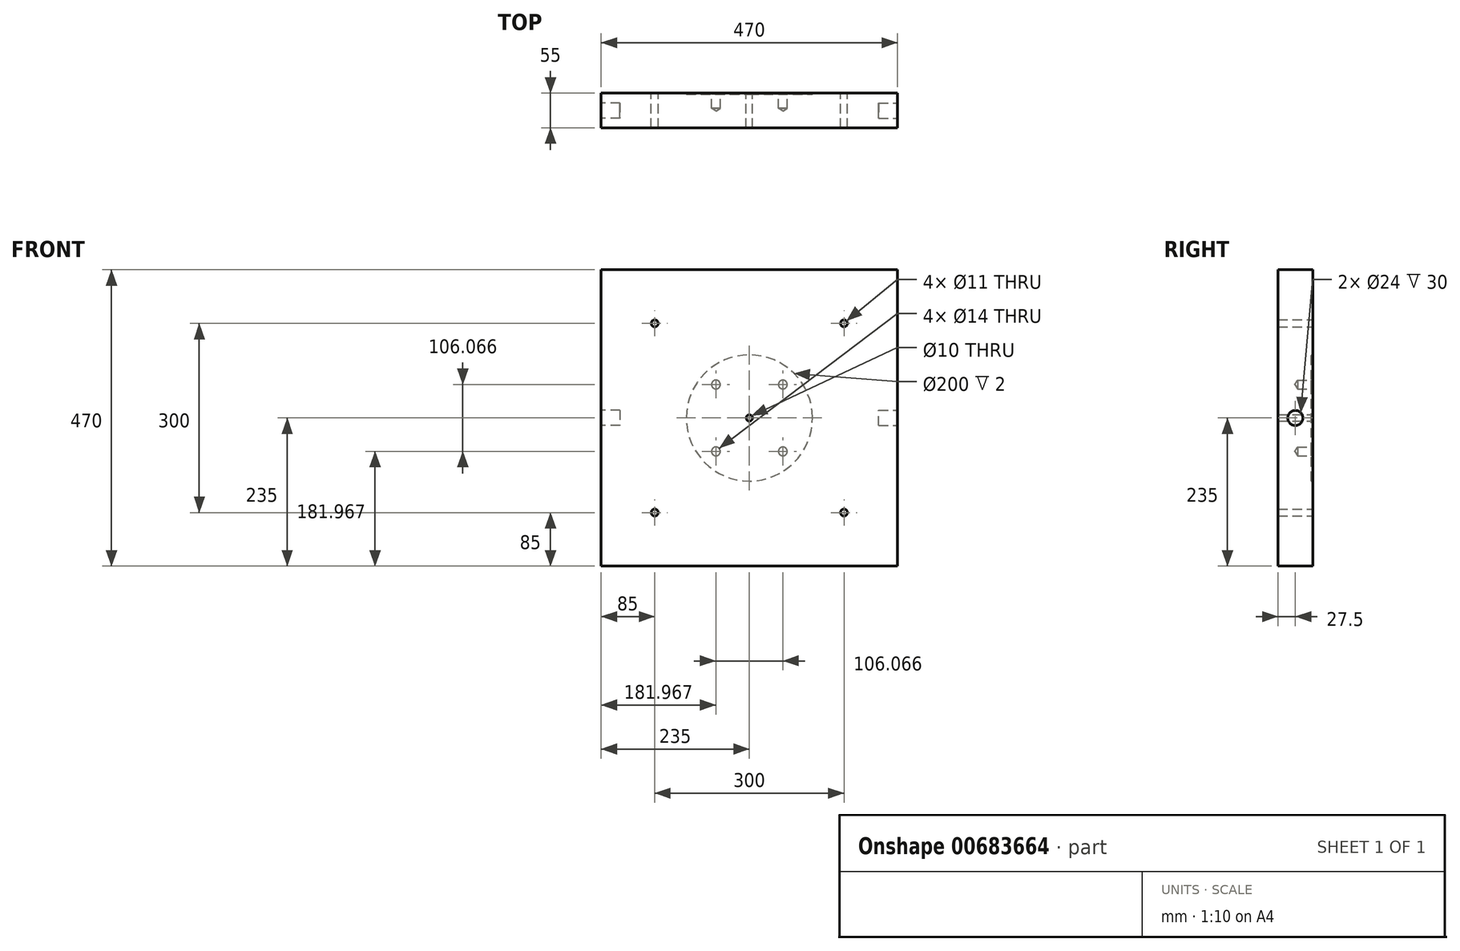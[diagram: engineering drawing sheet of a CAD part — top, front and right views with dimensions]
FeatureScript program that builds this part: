
annotation { "Feature Type Name" : "Feature", "Feature Type Description" : "" }
export const myFeature = defineFeature(function(context is Context, id is Id, definition is map)
    precondition{}
    {
        {
            var Q0;
            Q0=qCreatedBy(makeId("Front.planeOp"),FACE);
            var sketch = newSketch(context, id + "F0", { "sketchPlane" : qUnion([Q0])});
            skLineSegment(sketch, "E0.bottom", {"start": v(235, 235) * mm, "end": v(-235, 235) * mm});
            skLineSegment(sketch, "E0.top", {"start": v(235, -235) * mm, "end": v(-235, -235) * mm});
            skLineSegment(sketch, "E0.left", {"start": v(235, 235) * mm, "end": v(235, -235) * mm});
            skLineSegment(sketch, "E0.right", {"start": v(-235, 235) * mm, "end": v(-235, -235) * mm});
            skPoint(sketch, "E0.middle", {"position": v(0, 0) * mm});
            skCircle(sketch, "E1", {"center": v(0, 0) * mm, "radius": 5 * mm});
            skCircle(sketch, "E2", {"center": v(-150, 150) * mm, "radius": 5.5 * mm});
            skCircle(sketch, "E3", {"center": v(150, 150) * mm, "radius": 5.5 * mm});
            skCircle(sketch, "E4.MirrorC", {"center": v(150, -150) * mm, "radius": 5.5 * mm});
            skCircle(sketch, "E5.MirrorC", {"center": v(-150, -150) * mm, "radius": 5.5 * mm});
            skLineSegment(sketch, "E6", {"start": v(0, 0) * mm, "end": v(53.03, 53.03) * mm, "construction": true});
            skPoint(sketch, "E7", {"position": v(53.03, 53.03) * mm});
            skPoint(sketch, "E8.MirrorP", {"position": v(-53.03, 53.03) * mm});
            skPoint(sketch, "E9.MirrorP", {"position": v(53.03, -53.03) * mm});
            skPoint(sketch, "E10.MirrorP", {"position": v(-53.03, -53.03) * mm});
            skSolve(sketch);
        }
        {
            var Q0;
            Q0=makeQuery(id+"F0.imprint","IMPRINT",FACE,{"disambiguationData":[TD([[makeQuery(id+"F0.imprint","IMPRINT",EDGE,{"derivedFrom":sQuery(id+"F0.wireOp",EDGE,"E0.bottom")}),1.0]])]});
            extrude(context, id + "F1", {"entities" : qUnion([Q0]), "depth" : 55 * mm, "offsetDistance" : 25 * mm});
        }
        {
            var Q0;
            Q0=sQuery(id+"F0.wireOp",VERTEX,"E7");
            var Q1;
            Q1=sQuery(id+"F0.wireOp",VERTEX,"E8.MirrorP");
            var Q2;
            Q2=sQuery(id+"F0.wireOp",VERTEX,"E10.MirrorP");
            var Q3;
            Q3=sQuery(id+"F0.wireOp",VERTEX,"E9.MirrorP");
            var Q4;
            Q4=makeQuery(id+"F1.opExtrude","SWEPT_BODY",BODY,{"disambiguationData":[OSD([sQuery(id+"F0.wireOp",EDGE,"E0.bottom"),sQuery(id+"F0.wireOp",EDGE,"E0.top"),sQuery(id+"F0.wireOp",EDGE,"E0.left"),sQuery(id+"F0.wireOp",EDGE,"E0.right"),sQuery(id+"F0.wireOp",EDGE,"E1"),sQuery(id+"F0.wireOp",EDGE,"E2"),sQuery(id+"F0.wireOp",EDGE,"E3"),sQuery(id+"F0.wireOp",EDGE,"E4.MirrorC"),sQuery(id+"F0.wireOp",EDGE,"E5.MirrorC")])]});
            hole(context, id + "F2", {"style" : HoleStyle.SIMPLE, "endStyle" : HoleEndStyle.BLIND, "oppositeDirection" : true, "standardTappedOrClearance" : lookupTablePath({ "standard" : "ISO", "engagement" : "75%", "pitch" : "2 mm", "size" : "M16", "type" : "Tapped" }), "standardBlindInLast" : lookupTablePath({ "standard" : "ISO", "engagement" : "75%", "pitch" : "2 mm", "size" : "M16", "type" : "Tapped" }), "holeDiameter" : 14 * mm, "majorDiameter" : 16 * mm, "showTappedDepth" : true, "holeDepth" : 24 * mm, "isTappedThrough" : true, "tappedDepth" : 20 * mm, "tapClearance" : 2, "locations" : qUnion([Q0, Q1, Q2, Q3]), "scope" : qUnion([Q4])});
        }
        {
            var Q0;
            Q0=makeQuery(id+"F0.imprint","IMPRINT",FACE,{"disambiguationData":[TD([[makeQuery(id+"F0.imprint","IMPRINT",EDGE,{"derivedFrom":sQuery(id+"F0.wireOp",EDGE,"E0.bottom")}),1.0]])]});
            var sketch = newSketch(context, id + "F3", { "sketchPlane" : qUnion([Q0])});
            skCircle(sketch, "E11", {"center": v(0, 0) * mm, "radius": 100 * mm});
            skSolve(sketch);
        }
        {
            var Q0;
            Q0=makeQuery(id+"F3.imprint","IMPRINT",FACE,{"disambiguationData":[TD([[makeQuery(id+"F3.imprint","IMPRINT",EDGE,{"derivedFrom":sQuery(id+"F3.wireOp",EDGE,"E11")}),1.0]])]});
            extrude(context, id + "F4", {"entities" : qUnion([Q0]), "operationType" : NewBodyOperationType.REMOVE, "depth" : 2 * mm, "offsetDistance" : 25 * mm});
        }
        {
            var Q0;
            Q0=makeQuery(id+"F1.opExtrude","SWEPT_FACE",FACE,{"disambiguationData":[OSD([sQuery(id+"F0.wireOp",EDGE,"E0.left")])]});
            var sketch = newSketch(context, id + "F5", { "sketchPlane" : qUnion([Q0])});
            skPoint(sketch, "E12", {"position": v(-27.5, 0) * mm});
            skCircle(sketch, "E13", {"center": v(-27.5, 0) * mm, "radius": 12 * mm});
            skSolve(sketch);
        }
        {
            var Q0;
            Q0=makeQuery(id+"F5.imprint","IMPRINT",FACE,{"disambiguationData":[TD([[makeQuery(id+"F5.imprint","IMPRINT",EDGE,{"derivedFrom":sQuery(id+"F5.wireOp",EDGE,"E13")}),1.0]])]});
            extrude(context, id + "F6", {"entities" : qUnion([Q0]), "operationType" : NewBodyOperationType.REMOVE, "oppositeDirection" : true, "depth" : 30 * mm, "offsetDistance" : 25 * mm});
        }
        {
            var Q0;
            Q0=makeQuery(id+"F1.opExtrude","SWEPT_FACE",FACE,{"disambiguationData":[OSD([sQuery(id+"F0.wireOp",EDGE,"E0.right")])]});
            var sketch = newSketch(context, id + "F7", { "sketchPlane" : qUnion([Q0])});
            skCircle(sketch, "E14", {"center": v(27.5, 0) * mm, "radius": 12 * mm});
            skSolve(sketch);
        }
        {
            var Q0;
            Q0=makeQuery(id+"F7.imprint","IMPRINT",FACE,{"disambiguationData":[TD([[makeQuery(id+"F7.imprint","IMPRINT",EDGE,{"derivedFrom":sQuery(id+"F7.wireOp",EDGE,"E14")}),1.0]])]});
            extrude(context, id + "F8", {"entities" : qUnion([Q0]), "operationType" : NewBodyOperationType.REMOVE, "oppositeDirection" : true, "depth" : 30 * mm, "offsetDistance" : 25 * mm});
        }
    });
